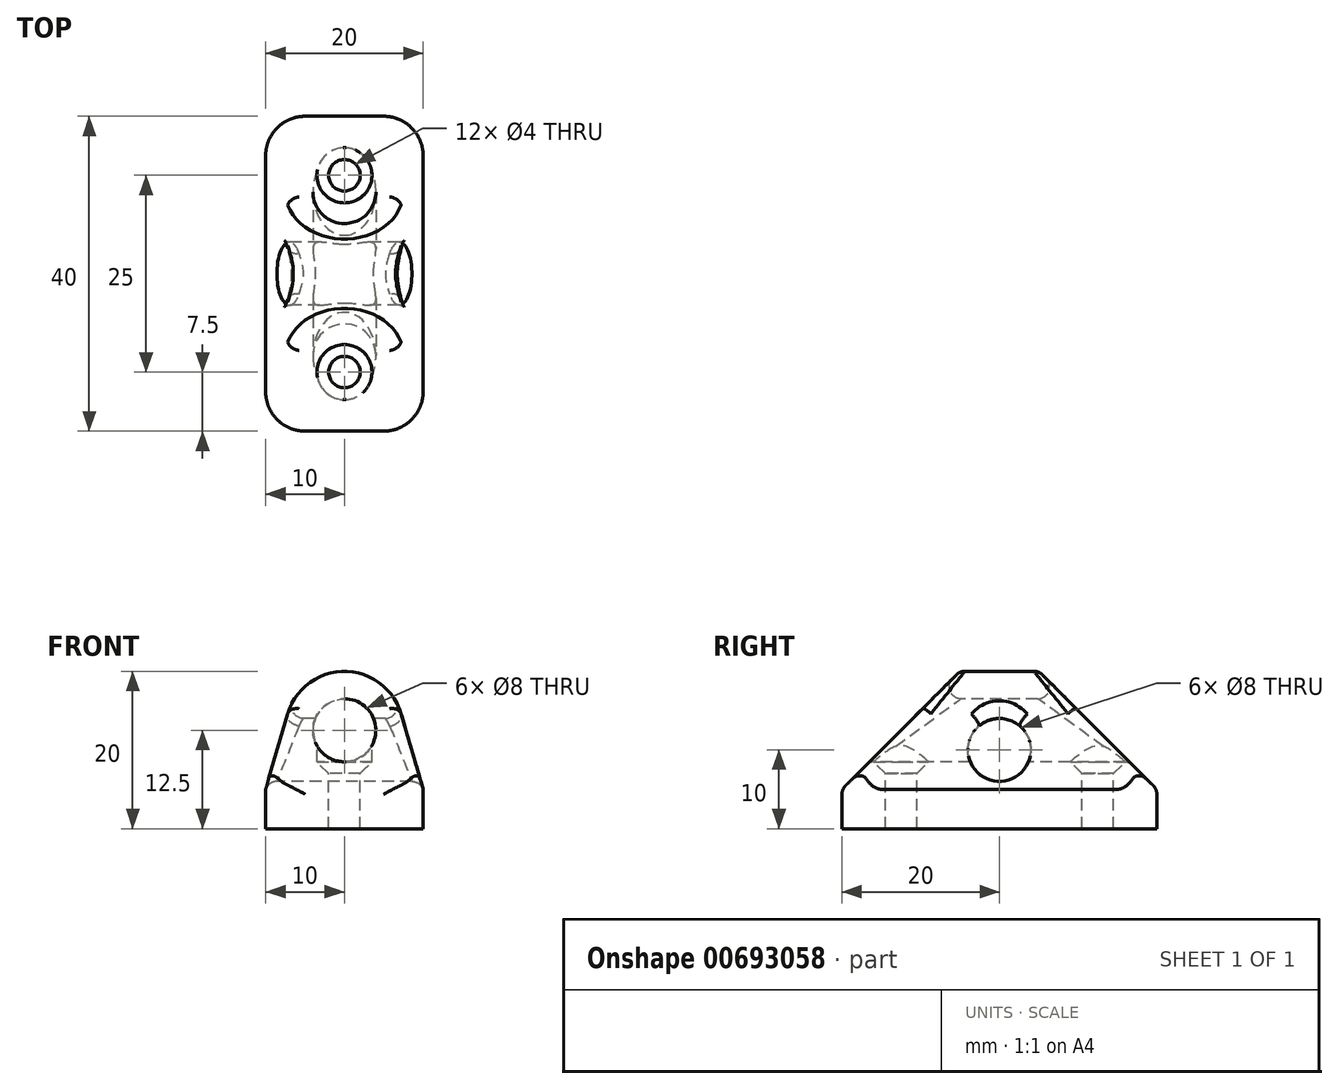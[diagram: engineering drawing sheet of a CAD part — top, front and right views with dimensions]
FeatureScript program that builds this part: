
annotation { "Feature Type Name" : "Feature", "Feature Type Description" : "" }
export const myFeature = defineFeature(function(context is Context, id is Id, definition is map)
    precondition{}
    {
        {
            var Q0;
            Q0=qCreatedBy(makeId("Right.planeOp"),FACE);
            var sketch = newSketch(context, id + "F0", { "sketchPlane" : qUnion([Q0])});
            skLineSegment(sketch, "E0", {"start": v(-20, 0) * mm, "end": v(20, 0) * mm});
            skLineSegment(sketch, "E1", {"start": v(20, 0) * mm, "end": v(20, 5) * mm});
            skLineSegment(sketch, "E2", {"start": v(20, 5) * mm, "end": v(5, 20) * mm});
            skLineSegment(sketch, "E3", {"start": v(5, 20) * mm, "end": v(-5, 20) * mm});
            skLineSegment(sketch, "E4", {"start": v(-5, 20) * mm, "end": v(-20, 5) * mm});
            skLineSegment(sketch, "E5", {"start": v(-20, 5) * mm, "end": v(-20, 0) * mm});
            skPoint(sketch, "E6", {"position": v(0, 20) * mm});
            skPoint(sketch, "E7", {"position": v(0, 0) * mm});
            skSolve(sketch);
        }
        {
            var Q0;
            Q0=makeQuery(id+"F0.imprint","IMPRINT",FACE,{"disambiguationData":[TD([[makeQuery(id+"F0.imprint","IMPRINT",EDGE,{"derivedFrom":sQuery(id+"F0.wireOp",EDGE,"E0")}),1.0]])]});
            extrude(context, id + "F1", {"entities" : qUnion([Q0]), "depth" : 20 * mm, "offsetDistance" : 25 * mm, "symmetric" : true});
        }
        {
            var Q0;
            Q0=makeQuery(id+"F1.opExtrude","CAP_FACE",FACE,{"disambiguationData":[OSD([sQuery(id+"F0.wireOp",EDGE,"E0"),sQuery(id+"F0.wireOp",EDGE,"E1"),sQuery(id+"F0.wireOp",EDGE,"E2"),sQuery(id+"F0.wireOp",EDGE,"E3"),sQuery(id+"F0.wireOp",EDGE,"E4"),sQuery(id+"F0.wireOp",EDGE,"E5")])],"isStart":true});
            var sketch = newSketch(context, id + "F2", { "sketchPlane" : qUnion([Q0])});
            skCircle(sketch, "E8", {"center": v(0, 10) * mm, "radius": 4 * mm});
            skSolve(sketch);
        }
        {
            var Q0;
            Q0 = qSketchRegion(id + "F2", true);
            extrude(context, id + "F3", {"entities" : qUnion([Q0]), "operationType" : NewBodyOperationType.REMOVE, "endBound" : BoundingType.THROUGH_ALL, "oppositeDirection" : true, "depth" : 25 * mm, "offsetDistance" : 25 * mm});
        }
        {
            var Q0;
            Q0=qCreatedBy(makeId("Front.planeOp"),FACE);
            var sketch = newSketch(context, id + "F4", { "sketchPlane" : qUnion([Q0])});
            skCircle(sketch, "E9", {"center": v(0, 12.5) * mm, "radius": 4 * mm});
            skPoint(sketch, "E10.0", {"position": v(10, 5) * mm});
            skPoint(sketch, "E10.1", {"position": v(-10, 5) * mm});
            skPoint(sketch, "E10.2", {"position": v(0, 20) * mm});
            skLineSegment(sketch, "E11", {"start": v(-10, 5) * mm, "end": v(-7.2, 14.6) * mm});
            skLineSegment(sketch, "E12", {"start": v(10, 5) * mm, "end": v(7.2, 14.6) * mm});
            skArc(sketch, "E13", {"start": v(7.2, 14.6) * mm, "mid": v(0, 20) * mm, "end": v(-7.2, 14.6) * mm});
            skArc(sketch, "E14", {"start": v(-7.2, 14.6) * mm, "mid": v(0, 5) * mm, "end": v(7.2, 14.6) * mm, "construction": true});
            skLineSegment(sketch, "E15", {"start": v(10, 5) * mm, "end": v(14.29, 5) * mm});
            skLineSegment(sketch, "E16", {"start": v(14.29, 5) * mm, "end": v(14.29, 24.43) * mm});
            skLineSegment(sketch, "E17", {"start": v(14.29, 24.43) * mm, "end": v(-13.26, 24.43) * mm});
            skLineSegment(sketch, "E18", {"start": v(-13.26, 24.43) * mm, "end": v(-13.26, 5) * mm});
            skLineSegment(sketch, "E19", {"start": v(-13.26, 5) * mm, "end": v(-10, 5) * mm});
            skSolve(sketch);
        }
        {
            var Q0;
            Q0=makeQuery(id+"F4.imprint","IMPRINT",FACE,{"disambiguationData":[TD([[makeQuery(id+"F4.imprint","IMPRINT",EDGE,{"derivedFrom":sQuery(id+"F4.wireOp",EDGE,"E9")}),1.0]])]});
            var Q1;
            Q1=makeQuery(id+"F4.imprint","IMPRINT",FACE,{"disambiguationData":[TD([[makeQuery(id+"F4.imprint","IMPRINT",EDGE,{"derivedFrom":sQuery(id+"F4.wireOp",EDGE,"E11")}),1.0]])]});
            extrude(context, id + "F5", {"entities" : qUnion([Q0, Q1]), "operationType" : NewBodyOperationType.REMOVE, "oppositeDirection" : true, "depth" : 50 * mm, "offsetDistance" : 25 * mm, "symmetric" : true});
        }
        {
            var Q0;
            Q0=qCreatedBy(makeId("Top.planeOp"),FACE);
            cPlane(context, id + "F6", {"entities" : qUnion([Q0]), "cplaneType" : CPlaneType.OFFSET, "offset" : 25 * mm, "width" : 150 * mm, "height" : 150 * mm});
        }
        {
            var Q0;
            Q0=qCreatedBy(id+"F6.planeOp",FACE);
            var sketch = newSketch(context, id + "F7", { "sketchPlane" : qUnion([Q0])});
            skCircle(sketch, "E20.0", {"center": v(0, 12.5) * mm, "radius": 4 * mm, "construction": true});
            skCircle(sketch, "E21.0", {"center": v(0, -12.5) * mm, "radius": 4 * mm, "construction": true});
            skSolve(sketch);
        }
        {
            var Q0;
            Q0=sQuery(id+"F7.wireOp",VERTEX,"E21.0.center");
            var Q1;
            Q1=sQuery(id+"F7.wireOp",VERTEX,"E20.0.center");
            var Q2;
            Q2=makeQuery(id+"F1.opExtrude","SWEPT_BODY",BODY,{"disambiguationData":[OSD([sQuery(id+"F0.wireOp",EDGE,"E0"),sQuery(id+"F0.wireOp",EDGE,"E1"),sQuery(id+"F0.wireOp",EDGE,"E2"),sQuery(id+"F0.wireOp",EDGE,"E3"),sQuery(id+"F0.wireOp",EDGE,"E4"),sQuery(id+"F0.wireOp",EDGE,"E5")])]});
            hole(context, id + "F8", {"style" : HoleStyle.C_SINK, "endStyle" : HoleEndStyle.BLIND, "holeDiameter" : 4 * mm, "cSinkDiameter" : 7 * mm, "cSinkAngle" : 90 * degree, "majorDiameter" : 5 * mm, "holeDepth" : 21 * mm, "isTappedThrough" : true, "tappedDepth" : 12 * mm, "tapClearance" : 3, "locations" : qUnion([Q0, Q1]), "scope" : qUnion([Q2])});
        }
        {
            var Q0;
            Q0=makeQuery(id+"F1.opExtrude","SWEPT_FACE",FACE,{"disambiguationData":[OSD([sQuery(id+"F0.wireOp",EDGE,"E2")])]});
            var Q1;
            Q1=makeQuery(id+"F1.opExtrude","SWEPT_FACE",FACE,{"disambiguationData":[OSD([sQuery(id+"F0.wireOp",EDGE,"E4")])]});
            var Q2;
            Q2=makeQuery(id+"F5.boolean.opBoolean","INTERSECT",EDGE,{"derivedFrom":[makeQuery(id+"F3.boolean.opBoolean","COPY",FACE,{"derivedFrom":makeQuery(id+"F3.opExtrude","SWEPT_FACE",FACE,{"disambiguationData":[OSD([sQuery(id+"F2.wireOp",EDGE,"E8")])]})}),makeQuery(id+"F5.opExtrude","SWEPT_FACE",FACE,{"disambiguationData":[OSD([sQuery(id+"F4.wireOp",EDGE,"E11")])]})]});
            var Q3;
            Q3=makeQuery(id+"F5.boolean.opBoolean","INTERSECT",EDGE,{"derivedFrom":[makeQuery(id+"F3.boolean.opBoolean","COPY",FACE,{"derivedFrom":makeQuery(id+"F3.opExtrude","SWEPT_FACE",FACE,{"disambiguationData":[OSD([sQuery(id+"F2.wireOp",EDGE,"E8")])]})}),makeQuery(id+"F5.opExtrude","SWEPT_FACE",FACE,{"disambiguationData":[OSD([sQuery(id+"F4.wireOp",EDGE,"E12")])]})]});
            fillet(context, id + "F9", {"entities" : qUnion([Q0, Q1, Q2, Q3]), "radius" : 1.5 * mm, "tangentPropagation" : true, "allowEdgeOverflow" : false});
        }
        {
            var Q0;
            Q0=makeQuery(id+"F1.opExtrude","CAP_EDGE",EDGE,{"disambiguationData":[OSD([sQuery(id+"F0.wireOp",EDGE,"E5")])],"isStart":false});
            var Q1;
            Q1=makeQuery(id+"F1.opExtrude","CAP_EDGE",EDGE,{"disambiguationData":[OSD([sQuery(id+"F0.wireOp",EDGE,"E5")])],"isStart":true});
            var Q2;
            Q2=makeQuery(id+"F1.opExtrude","CAP_EDGE",EDGE,{"disambiguationData":[OSD([sQuery(id+"F0.wireOp",EDGE,"E1")])],"isStart":true});
            var Q3;
            Q3=makeQuery(id+"F1.opExtrude","CAP_EDGE",EDGE,{"disambiguationData":[OSD([sQuery(id+"F0.wireOp",EDGE,"E1")])],"isStart":false});
            fillet(context, id + "F10", {"entities" : qUnion([Q0, Q1, Q2, Q3]), "radius" : 5 * mm, "tangentPropagation" : true, "allowEdgeOverflow" : false});
        }
    });
